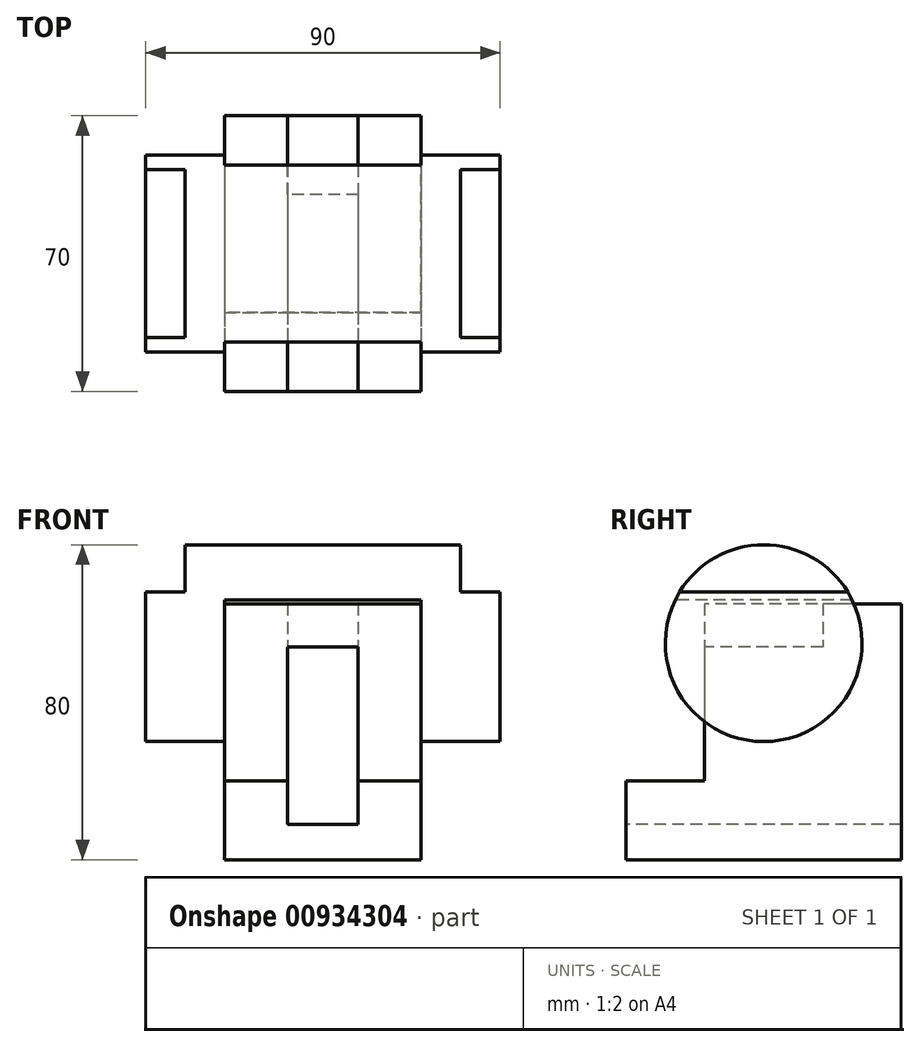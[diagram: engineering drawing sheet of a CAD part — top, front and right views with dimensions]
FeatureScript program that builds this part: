
annotation { "Feature Type Name" : "Feature", "Feature Type Description" : "" }
export const myFeature = defineFeature(function(context is Context, id is Id, definition is map)
    precondition{}
    {
        {
            var Q0;
            Q0=qCreatedBy(makeId("Front.planeOp"),FACE);
            var sketch = newSketch(context, id + "F0", { "sketchPlane" : qUnion([Q0])});
            skLineSegment(sketch, "E0", {"start": v(0, 0) * mm, "end": v(50, 0) * mm});
            skLineSegment(sketch, "E1", {"start": v(50, 0) * mm, "end": v(50, 20) * mm});
            skLineSegment(sketch, "E2", {"start": v(50, 20) * mm, "end": v(34, 20) * mm});
            skLineSegment(sketch, "E3", {"start": v(34, 20) * mm, "end": v(34, 9) * mm});
            skLineSegment(sketch, "E4", {"start": v(34, 9) * mm, "end": v(16, 9) * mm});
            skLineSegment(sketch, "E5", {"start": v(16, 9) * mm, "end": v(16, 20) * mm});
            skLineSegment(sketch, "E6", {"start": v(16, 20) * mm, "end": v(0, 20) * mm});
            skLineSegment(sketch, "E7", {"start": v(0, 20) * mm, "end": v(0, 0) * mm});
            skSolve(sketch);
        }
        {
            var Q0;
            Q0 = qSketchRegion(id + "F0", true);
            extrude(context, id + "F1", {"entities" : qUnion([Q0]), "oppositeDirection" : true, "depth" : 70 * mm, "offsetDistance" : 25 * mm});
        }
        {
            var Q0;
            Q0=makeQuery(id+"F1.opExtrude","SWEPT_FACE",FACE,{"disambiguationData":[OSD([sQuery(id+"F0.wireOp",EDGE,"E6")])]});
            var sketch = newSketch(context, id + "F2", { "sketchPlane" : qUnion([Q0])});
            skLineSegment(sketch, "E8.bottom", {"start": v(0, 70) * mm, "end": v(16, 70) * mm});
            skLineSegment(sketch, "E8.top", {"start": v(0, 20) * mm, "end": v(16, 20) * mm});
            skLineSegment(sketch, "E8.left", {"start": v(0, 70) * mm, "end": v(0, 20) * mm});
            skLineSegment(sketch, "E8.right", {"start": v(16, 70) * mm, "end": v(16, 20) * mm});
            skLineSegment(sketch, "E9.bottom", {"start": v(34, 70) * mm, "end": v(50, 70) * mm});
            skLineSegment(sketch, "E9.top", {"start": v(34, 20) * mm, "end": v(50, 20) * mm});
            skLineSegment(sketch, "E9.left", {"start": v(34, 70) * mm, "end": v(34, 20) * mm});
            skLineSegment(sketch, "E9.right", {"start": v(50, 70) * mm, "end": v(50, 20) * mm});
            skSolve(sketch);
        }
        {
            var Q0;
            Q0=makeQuery(id+"F2.imprint","IMPRINT",FACE,{"disambiguationData":[TD([[makeQuery(id+"F2.imprint","IMPRINT",EDGE,{"derivedFrom":sQuery(id+"F2.wireOp",EDGE,"E8.bottom")}),1.0]])]});
            var Q1;
            Q1=makeQuery(id+"F2.imprint","IMPRINT",FACE,{"disambiguationData":[TD([[makeQuery(id+"F2.imprint","IMPRINT",EDGE,{"derivedFrom":sQuery(id+"F2.wireOp",EDGE,"E9.bottom")}),-1.0]])]});
            extrude(context, id + "F3", {"entities" : qUnion([Q0, Q1]), "operationType" : NewBodyOperationType.ADD, "depth" : 45 * mm, "offsetDistance" : 25 * mm});
        }
        {
            var Q0;
            Q0=makeQuery(id+"F3.boolean.opBoolean","MERGE",FACE,{"derivedFrom":[makeQuery(id+"F1.opExtrude","SWEPT_FACE",FACE,{"disambiguationData":[OSD([sQuery(id+"F0.wireOp",EDGE,"E7")])]}),makeQuery(id+"F3.opExtrude","SWEPT_FACE",FACE,{"disambiguationData":[OSD([sQuery(id+"F2.wireOp",EDGE,"E8.left")])]})]});
            var sketch = newSketch(context, id + "F4", { "sketchPlane" : qUnion([Q0])});
            skCircle(sketch, "E10", {"center": v(-35, 55) * mm, "radius": 25 * mm});
            skSolve(sketch);
        }
        {
            var Q0;
            {var subQ0=sQuery(id+"F4.wireOp",EDGE,"E10");var subQ1=sQuery(id+"F2.wireOp",EDGE,"E8.left");var subQ4=makeQuery(id+"F3.opExtrude","CAP_EDGE",EDGE,{"disambiguationData":[OSD([subQ1])],"isStart":false});var subQ5=makeQuery(id+"F4.imprint","INTERSECT",VERTEX,{"derivedFrom":[subQ4,subQ0]});Q0=makeQuery(id+"F4.imprint","IMPRINT",FACE,{"disambiguationData":[TD([[makeQuery(id+"F4.imprint","IMPRINT",EDGE,{"disambiguationData":[TD([[subQ5,1.0]])],"derivedFrom":subQ0}),1.0]])]});}
            var Q1;
            {var subQ0=sQuery(id+"F4.wireOp",EDGE,"E10");var subQ1=sQuery(id+"F2.wireOp",EDGE,"E8.left");var subQ4=makeQuery(id+"F3.opExtrude","CAP_EDGE",EDGE,{"disambiguationData":[OSD([subQ1])],"isStart":false});var subQ5=makeQuery(id+"F4.imprint","INTERSECT",VERTEX,{"derivedFrom":[subQ4,subQ0]});Q1=makeQuery(id+"F4.imprint","IMPRINT",FACE,{"disambiguationData":[TD([[makeQuery(id+"F4.imprint","IMPRINT",EDGE,{"disambiguationData":[TD([[subQ5,-1.0]])],"derivedFrom":subQ0}),1.0]])]});}
            extrude(context, id + "F5", {"entities" : qUnion([Q0, Q1]), "operationType" : NewBodyOperationType.ADD, "depth" : 20 * mm, "offsetDistance" : 25 * mm});
        }
        {
            var Q0;
            Q0=makeQuery(id+"F5.opExtrude","CAP_FACE",FACE,{"disambiguationData":[OSD([sQuery(id+"F4.wireOp",EDGE,"E10")])],"isStart":false});
            extrude(context, id + "F6", {"entities" : qUnion([Q0]), "operationType" : NewBodyOperationType.ADD, "oppositeDirection" : true, "depth" : 90 * mm, "offsetDistance" : 25 * mm});
        }
        {
            var Q0;
            Q0=makeQuery(id+"F5.opExtrude","CAP_FACE",FACE,{"disambiguationData":[OSD([sQuery(id+"F4.wireOp",EDGE,"E10")])],"isStart":false});
            var sketch = newSketch(context, id + "F7", { "sketchPlane" : qUnion([Q0])});
            skLineSegment(sketch, "E11", {"start": v(-57.46, 65.99) * mm, "end": v(-12.54, 65.99) * mm});
            skSolve(sketch);
        }
        {
            var Q0;
            {var subQ0=sQuery(id+"F7.wireOp",EDGE,"E11");Q0=makeQuery(id+"F7.imprint","IMPRINT",FACE,{"disambiguationData":[TD([[makeQuery(id+"F7.imprint","IMPRINT",EDGE,{"derivedFrom":subQ0}),-1.0]])]});}
            var sketch = newSketch(context, id + "F8", { "sketchPlane" : qUnion([Q0])});
            skLineSegment(sketch, "E12", {"start": v(-35.12, 68) * mm, "end": v(-35.12, 30) * mm});
            skSolve(sketch);
        }
        {
            var Q0;
            {var subQ0=sQuery(id+"F7.wireOp",EDGE,"E11");Q0=makeQuery(id+"F7.imprint","IMPRINT",FACE,{"disambiguationData":[TD([[makeQuery(id+"F7.imprint","IMPRINT",EDGE,{"derivedFrom":subQ0}),1.0]])]});}
            var sketch = newSketch(context, id + "F9", { "sketchPlane" : qUnion([Q0])});
            skLineSegment(sketch, "E13", {"start": v(-56.35, 68) * mm, "end": v(-13.65, 68) * mm});
            skSolve(sketch);
        }
        {
            var Q0;
            {var subQ0=sQuery(id+"F9.wireOp",EDGE,"E13");Q0=makeQuery(id+"F9.imprint","IMPRINT",FACE,{"disambiguationData":[TD([[makeQuery(id+"F9.imprint","IMPRINT",EDGE,{"derivedFrom":subQ0}),1.0]])]});}
            extrude(context, id + "F10", {"entities" : qUnion([Q0]), "operationType" : NewBodyOperationType.REMOVE, "oppositeDirection" : true, "depth" : 10 * mm, "offsetDistance" : 25 * mm});
        }
        {
            var Q0;
            Q0=makeQuery(id+"F6.opExtrude","CAP_FACE",FACE,{"disambiguationData":[OSD([sQuery(id+"F4.wireOp",EDGE,"E10")])],"isStart":false});
            var sketch = newSketch(context, id + "F11", { "sketchPlane" : qUnion([Q0])});
            skLineSegment(sketch, "E14", {"start": v(13.65, 68) * mm, "end": v(56.35, 68) * mm});
            skSolve(sketch);
        }
        {
            var Q0;
            {var subQ0=sQuery(id+"F11.wireOp",EDGE,"E14");Q0=makeQuery(id+"F11.imprint","IMPRINT",FACE,{"disambiguationData":[TD([[makeQuery(id+"F11.imprint","IMPRINT",EDGE,{"derivedFrom":subQ0}),1.0]])]});}
            extrude(context, id + "F12", {"entities" : qUnion([Q0]), "operationType" : NewBodyOperationType.REMOVE, "oppositeDirection" : true, "depth" : 10 * mm, "offsetDistance" : 25 * mm});
        }
        {
            var Q0;
            {var subQ0=sQuery(id+"F8.wireOp",EDGE,"E12");var subQ1=sQuery(id+"F7.wireOp",EDGE,"E11");var subQ5=makeQuery(id+"F7.imprint","IMPRINT",EDGE,{"derivedFrom":subQ1});var subQ6=makeQuery(id+"F8.imprint","INTERSECT",VERTEX,{"derivedFrom":[subQ5,subQ0]});Q0=makeQuery(id+"F8.imprint","IMPRINT",FACE,{"disambiguationData":[TD([[makeQuery(id+"F8.imprint","IMPRINT",EDGE,{"disambiguationData":[TD([[subQ6,-1.0]])],"derivedFrom":subQ0}),1.0]])]});}
            var Q1;
            {var subQ0=sQuery(id+"F8.wireOp",EDGE,"E12");var subQ1=sQuery(id+"F7.wireOp",EDGE,"E11");var subQ5=makeQuery(id+"F7.imprint","IMPRINT",EDGE,{"derivedFrom":subQ1});var subQ6=makeQuery(id+"F8.imprint","INTERSECT",VERTEX,{"derivedFrom":[subQ5,subQ0]});Q1=makeQuery(id+"F8.imprint","IMPRINT",FACE,{"disambiguationData":[TD([[makeQuery(id+"F8.imprint","IMPRINT",EDGE,{"disambiguationData":[TD([[subQ6,-1.0]])],"derivedFrom":subQ0}),-1.0]])]});}
            extrude(context, id + "F13", {"entities" : qUnion([Q0, Q1]), "operationType" : NewBodyOperationType.REMOVE, "oppositeDirection" : true, "depth" : 20 * mm, "offsetDistance" : 25 * mm});
        }
        {
            var Q0;
            Q0=makeQuery(id+"F13.boolean.opBoolean","MERGE",FACE,{"derivedFrom":[makeQuery(id+"F3.boolean.opBoolean","MERGE",FACE,{"derivedFrom":[makeQuery(id+"F1.opExtrude","SWEPT_FACE",FACE,{"disambiguationData":[OSD([sQuery(id+"F0.wireOp",EDGE,"E7")])]}),makeQuery(id+"F3.opExtrude","SWEPT_FACE",FACE,{"disambiguationData":[OSD([sQuery(id+"F2.wireOp",EDGE,"E8.left")])]})]})],"fromTools":[makeQuery(id+"F13.opExtrude","CAP_FACE",FACE,{"disambiguationData":[OSD([sQuery(id+"F4.wireOp",EDGE,"E10"),sQuery(id+"F7.wireOp",EDGE,"E11")])],"isStart":false})]});
            var sketch = newSketch(context, id + "F14", { "sketchPlane" : qUnion([Q0])});
            skLineSegment(sketch, "E15", {"start": v(-20, 35) * mm, "end": v(-20, 65.99) * mm});
            skSolve(sketch);
        }
        {
            var Q0;
            {var subQ3=sQuery(id+"F14.wireOp",EDGE,"E15");Q0=makeQuery(id+"F14.imprint","IMPRINT",FACE,{"disambiguationData":[TD([[makeQuery(id+"F14.imprint","IMPRINT",EDGE,{"derivedFrom":subQ3}),1.0]])]});}
            var sketch = newSketch(context, id + "F15", { "sketchPlane" : qUnion([Q0])});
            skLineSegment(sketch, "E16", {"start": v(-70, 35) * mm, "end": v(-20, 35) * mm});
            skSolve(sketch);
        }
        {
            var Q0;
            {var subQ11=sQuery(id+"F15.wireOp",EDGE,"E16");Q0=makeQuery(id+"F15.imprint","IMPRINT",FACE,{"disambiguationData":[TD([[makeQuery(id+"F15.imprint","IMPRINT",EDGE,{"derivedFrom":subQ11}),1.0]])]});}
            var Q1;
            {var subQ0=sQuery(id+"F14.wireOp",EDGE,"E15");Q1=makeQuery(id+"F14.imprint","IMPRINT",FACE,{"disambiguationData":[TD([[makeQuery(id+"F14.imprint","IMPRINT",EDGE,{"derivedFrom":subQ0}),-1.0]])]});}
            extrude(context, id + "F16", {"entities" : qUnion([Q0, Q1]), "operationType" : NewBodyOperationType.REMOVE, "oppositeDirection" : true, "depth" : 50 * mm, "offsetDistance" : 25 * mm});
        }
        {
            var Q0;
            Q0=makeQuery(id+"F16.boolean.opBoolean","COPY",FACE,{"derivedFrom":makeQuery(id+"F16.opExtrude","SWEPT_FACE",FACE,{"disambiguationData":[OSD([sQuery(id+"F15.wireOp",EDGE,"E16")])]})});
            extrude(context, id + "F17", {"entities" : qUnion([Q0]), "operationType" : NewBodyOperationType.ADD, "depth" : 25 * mm, "offsetDistance" : 25 * mm});
        }
        {
            var Q0;
            Q0=makeQuery(id+"F17.opExtrude","CAP_FACE",FACE,{"disambiguationData":[OSD([sQuery(id+"F15.wireOp",EDGE,"E16")])],"isStart":false});
            extrude(context, id + "F18", {"entities" : qUnion([Q0]), "operationType" : NewBodyOperationType.ADD, "depth" : 5 * mm, "offsetDistance" : 25 * mm});
        }
        {
            var Q0;
            {var subQ0=sQuery(id+"F15.wireOp",EDGE,"E16");var subQ1=sQuery(id+"F14.wireOp",EDGE,"E15");var subQ2=sQuery(id+"F4.wireOp",EDGE,"E10");var subQ3=sQuery(id+"F2.wireOp",EDGE,"E9.top");var subQ4=sQuery(id+"F2.wireOp",EDGE,"E8.left");var subQ5=sQuery(id+"F2.wireOp",EDGE,"E8.top");var subQ6=sQuery(id+"F0.wireOp",EDGE,"E7");var subQ7=sQuery(id+"F0.wireOp",EDGE,"E6");Q0=makeQuery(id+"F18.boolean.opBoolean","MERGE",FACE,{"derivedFrom":[makeQuery(id+"F17.boolean.opBoolean","MERGE",FACE,{"derivedFrom":[makeQuery(id+"F3.opExtrude","SWEPT_FACE",FACE,{"disambiguationData":[OSD([subQ5])]}),makeQuery(id+"F3.opExtrude","SWEPT_FACE",FACE,{"disambiguationData":[OSD([subQ3])]}),makeQuery(id+"F17.opExtrude","SWEPT_FACE",FACE,{"disambiguationData":[OSD([subQ7,subQ6,subQ5,subQ4,subQ3,subQ2,subQ1,subQ0])]})]}),makeQuery(id+"F18.opExtrude","SWEPT_FACE",FACE,{"disambiguationData":[OSD([subQ7,subQ6,subQ5,subQ4,subQ3,subQ2,subQ1,subQ0])]})]});}
            var sketch = newSketch(context, id + "F19", { "sketchPlane" : qUnion([Q0])});
            skLineSegment(sketch, "E17.bottom", {"start": v(16, 54) * mm, "end": v(34, 54) * mm});
            skLineSegment(sketch, "E17.top", {"start": v(16, 35) * mm, "end": v(34, 35) * mm});
            skLineSegment(sketch, "E17.left", {"start": v(16, 54) * mm, "end": v(16, 35) * mm});
            skLineSegment(sketch, "E17.right", {"start": v(34, 54) * mm, "end": v(34, 35) * mm});
            skSolve(sketch);
        }
        {
            var Q0;
            Q0=makeQuery(id+"F19.imprint","IMPRINT",FACE,{"disambiguationData":[TD([[makeQuery(id+"F19.imprint","IMPRINT",EDGE,{"derivedFrom":sQuery(id+"F19.wireOp",EDGE,"E17.bottom")}),-1.0]])]});
            extrude(context, id + "F20", {"entities" : qUnion([Q0]), "operationType" : NewBodyOperationType.REMOVE, "endBound" : BoundingType.THROUGH_ALL, "oppositeDirection" : true, "depth" : 25 * mm, "offsetDistance" : 25 * mm});
        }
        {
            var Q0;
            Q0=makeQuery(id+"F20.boolean.opBoolean","COPY",FACE,{"derivedFrom":makeQuery(id+"F20.opExtrude","SWEPT_FACE",FACE,{"disambiguationData":[OSD([sQuery(id+"F19.wireOp",EDGE,"E17.top")])]})});
            extrude(context, id + "F21", {"entities" : qUnion([Q0]), "operationType" : NewBodyOperationType.REMOVE, "endBound" : BoundingType.UP_TO_NEXT, "oppositeDirection" : true, "depth" : 25 * mm, "offsetDistance" : 25 * mm});
        }
        {
            var Q0;
            {var subQ0=sQuery(id+"F7.wireOp",EDGE,"E11");Q0=makeQuery(id+"F7.imprint","IMPRINT",FACE,{"disambiguationData":[TD([[makeQuery(id+"F7.imprint","IMPRINT",EDGE,{"derivedFrom":subQ0}),-1.0]])]});}
            extrude(context, id + "F22", {"entities" : qUnion([Q0]), "operationType" : NewBodyOperationType.ADD, "oppositeDirection" : true, "depth" : 20 * mm, "offsetDistance" : 25 * mm});
        }
    });
